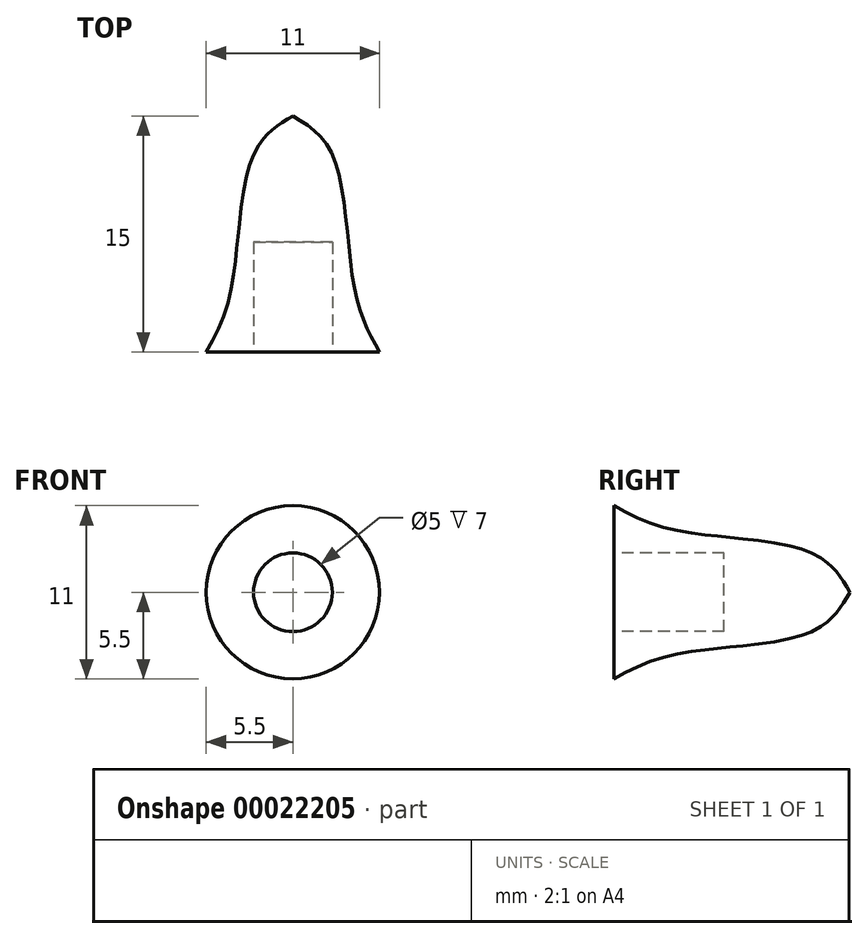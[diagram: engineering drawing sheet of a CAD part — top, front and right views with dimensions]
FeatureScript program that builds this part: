
annotation { "Feature Type Name" : "Feature", "Feature Type Description" : "" }
export const myFeature = defineFeature(function(context is Context, id is Id, definition is map)
    precondition{}
    {
        {
            var Q0;
            Q0=qCreatedBy(makeId("Top.planeOp"),FACE);
            var sketch = newSketch(context, id + "F0", { "sketchPlane" : qUnion([Q0])});
            skLineSegment(sketch, "E0.bottom", {"start": v(2.5, 0) * mm, "end": v(5.5, 0) * mm});
            skLineSegment(sketch, "E0.left", {"start": v(0, 7) * mm, "end": v(0, 15) * mm});
            skFitSpline(sketch, "E1", {"points": [v(0, 15) * mm, v(2.52, 12.51) * mm, v(3.9, 4.06) * mm, v(5.5, 0) * mm], "startDerivative": vector(10.66, -6.39) * mm, "endDerivative": vector(6.14, -11.17) * mm});
            skLineSegment(sketch, "E2.top", {"start": v(0, 7) * mm, "end": v(2.5, 7) * mm});
            skLineSegment(sketch, "E2.right", {"start": v(2.5, 0) * mm, "end": v(2.5, 7) * mm});
            skSolve(sketch);
        }
        {
            var Q0;
            Q0=qSketchRegion(id+"F0",true);
            var Q1;
            Q1=sQuery(id+"F0.wireOp",EDGE,"E0.left");
            revolve(context, id + "F1", {"entities" : qUnion([Q0]), "axis" : qUnion([Q1]), "revolveType" : RevolveType.FULL});
        }
    });
